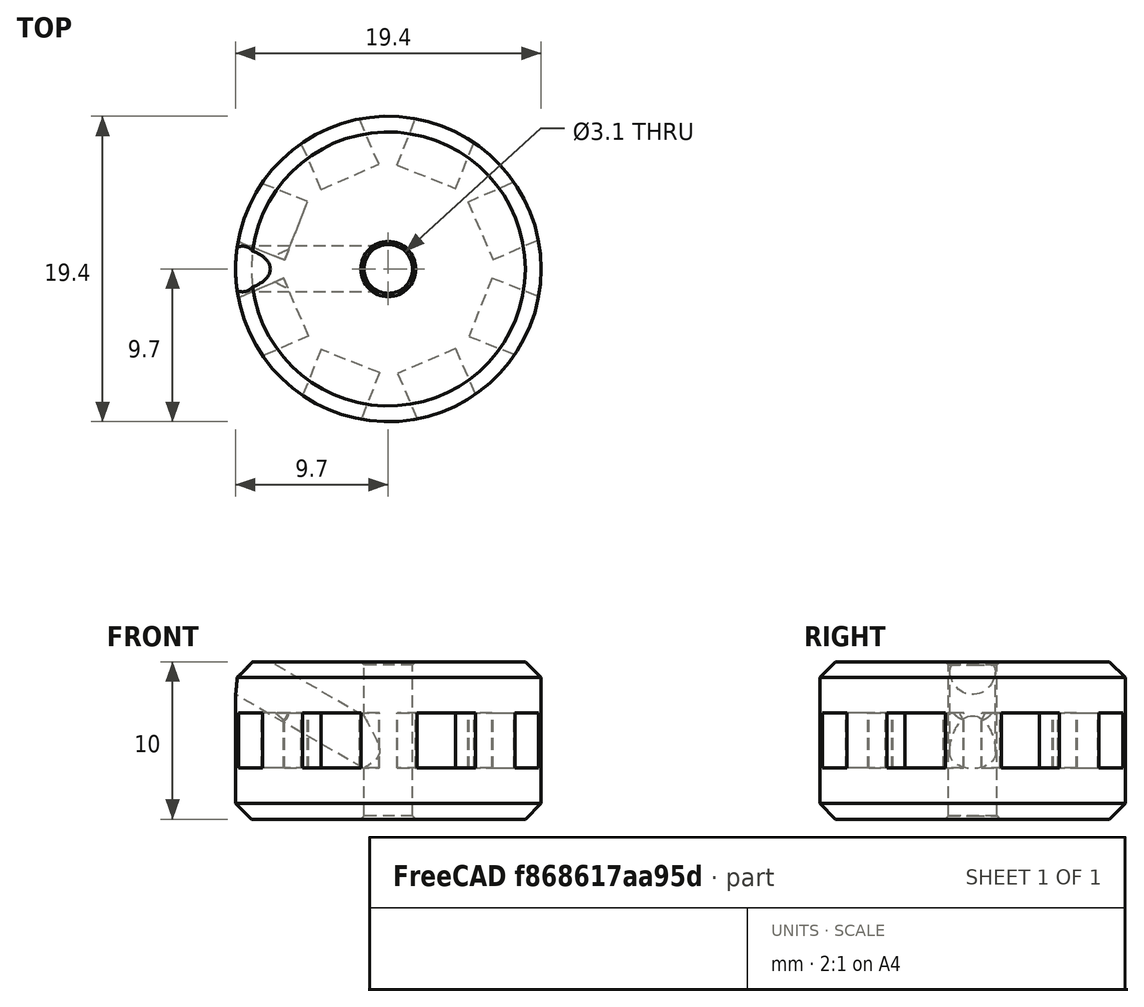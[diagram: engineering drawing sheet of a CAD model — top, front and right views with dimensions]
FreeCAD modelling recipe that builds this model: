
FCSTD DOCUMENT  (FreeCAD 0.17R13541 (Git))
Label: rueda8dientes
License: All rights reserved
LicenseURL: http://en.wikipedia.org/wiki/All_rights_reserved
objects: Part::Cylinder×3, Part::Chamfer×2, Part::Box×1, Part::FeaturePython×1, Part::MultiFuse×1, Part::Cut×1
note: 9 computed .brp shape members not serialized (recipe doc carries the construction recipe); baked Part::Feature solids carry a one-line shape summary decoded from their .brp

FEATURE [Part::Cylinder] Cylinder  label="Cilindro"
  Angle = 360
  AttacherType = Attacher::AttachEngine3D
  Height = 10
  Radius = 9.7
FEATURE [Part::Box] Box001  label="Cubo001"
  AttacherType = Attacher::AttachEngine3D
  Height = 3.5
  Length = 4
  Placement = pos=(-2,6.3,3.25) rot=(0,0,1;0.017453rad)
  Width = 10
FEATURE [Part::Cylinder] Cylinder002  label="eje"
  Angle = 360
  AttacherType = Attacher::AttachEngine3D
  Height = 20
  Radius = 1.55
FEATURE [Part::Cylinder] Cylinder004  label="tornillo"
  Angle = 360
  AttacherType = Attacher::AttachEngine3D
  Height = 50
  Placement = pos=(0,0,4) rot=(0,-1,0;1.0472rad)
  Radius = 1.45
FEATURE [Part::FeaturePython] Array  # Draft array (typed FeaturePython)
  Angle = 360
  ArrayType = 1
  Axis = (0,0,1)
  Base = -> Box001
  Center = (0,0,0)
  Fuse = false
  IntervalAxis = (0,0,0)
  IntervalX = (1,0,0)
  IntervalY = (0,1,0)
  IntervalZ = (0,0,0)
  NumberPolar = 8
  NumberX = 2
  NumberY = 2
  NumberZ = 1
  Placement = pos=(0,0,0) rot=(0,0,1;0.392699rad)
FEATURE [Part::Chamfer] Chamfer
  Base = -> Cylinder
  Edges = 2 edges r=1: [Edge1,Edge3]
FEATURE [Part::MultiFuse] Fusion
  Refine = true
  Shapes = -> [Cylinder002,Array,Cylinder004]
FEATURE [Part::Cut] Cut
  Base = -> Chamfer
  Refine = true
  Tool = -> Fusion
FEATURE [Part::Chamfer] Chamfer001
  Base = -> Cut
  Edges = 2 edges r=0.2: [Edge119,Edge120]
